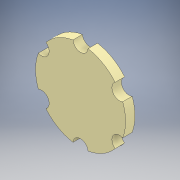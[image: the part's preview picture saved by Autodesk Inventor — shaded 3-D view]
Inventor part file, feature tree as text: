
AUTODESK INVENTOR PART (.ipt)
format: ipt  version: 2017 (Build 210142000, 142)  size: 134,656 bytes
history: native  units: mm
features: extrude x2, sketch x2
ambient origin geometry x8: Origin, YZ Plane, XZ Plane, XY Plane, X Axis, Y Axis, Z Axis, Center Point
bodies: Solid1 (feature_tree)
feature tree (4):
  extrude  "Extrusion1"  Depth=3.2mm
  extrude  "Extrusion2"  Depth=2.0mm TaperAngle=0.0deg
  sketch  "Sketch1"  dims[d0=19.0mm d1=3.2mm]
  sketch  "Sketch2"  dims[d2=60.0mm d4=360.0deg d6=2.0mm d7=0.0mm d8=4.0mm d9=4.0mm d10=2.0mm d11=0.0mm]
